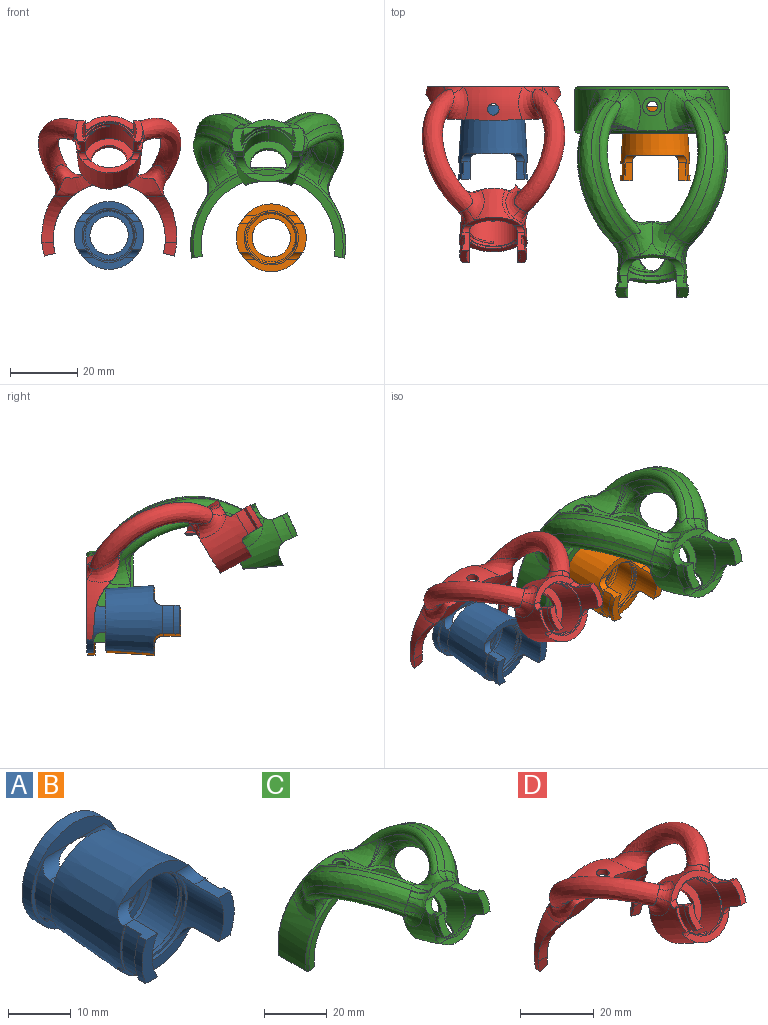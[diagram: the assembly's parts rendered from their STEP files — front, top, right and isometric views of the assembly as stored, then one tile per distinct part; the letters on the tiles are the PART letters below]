
ASSEMBLY  parts=4 mates=3
PART A: 50 faces, bbox 20.8x27.6x20.6 mm
  f0: cone r=10.29mm half-angle=3.8deg, axis (0,-1,0), area 925mm2, adj f1,f2,f13,f14,f30,f33,f40,f41
  f1: plane 8.53x1.35mm, normal (0,-1,0), area 3.4mm2, adj f0,f4,f41,f44
  f2: plane 8.53x1.35mm, normal (0,-1,0), area 3.4mm2, adj f0,f3,f40,f43
  f3: cylinder r=9.91mm len=8.53mm, axis (0,-1,0), area 30.3mm2, adj f2,f5,f40,f43
  f4: cylinder r=9.91mm len=8.53mm, axis (0,-1,0), area 30.3mm2, adj f1,f6,f41,f44
  f5: plane 8.53x1.47mm, normal (0,1,0), area 4.5mm2, adj f3,f7,f40,f43
  f6: plane 8.53x1.47mm, normal (0,1,0), area 4.5mm2, adj f4,f8,f41,f44
  f7: cylinder r=10.41mm len=8.53mm, axis (0,-1,0), area 14mm2, adj f5,f10,f40,f43
  f8: cylinder r=10.41mm len=8.53mm, axis (0,-1,0), area 14mm2, adj f6,f9,f41,f44
  f9: plane 8.53x3.56mm, normal (0,-1,0), area 20.7mm2, adj f8,f11,f41,f44
  f10: plane 8.53x3.56mm, normal (0,-1,0), area 20.7mm2, adj f7,f11,f40,f43
  f11: cylinder r=8.08mm len=16.15mm, axis (0,-1,0), area 174.9mm2, adj f9,f10,f18,f40,f41,f42,f43,f44
  f12: cone r=6.25mm half-angle=0.6deg, axis (0,1,0), area 332.4mm2, adj f15,f17,f26,f30,f31,f32,f33,f34
  f13: cylinder r=9.14mm len=12.62mm, axis (0,-1,0), area 30mm2, adj f0,f17,f32,f35,f36,f37
  f14: cylinder r=9.14mm len=12.62mm, axis (0,-1,0), area 30mm2, adj f0,f17,f31,f34,f38,f39
  f15: plane 19.81x19.81mm, normal (0,1,0), area 181.6mm2, adj f12,f16
  f16: cylinder r=9.91mm len=19.81mm, axis (0,-1,0), area 134.4mm2, adj f15,f17
  f17: plane 19.81x19.81mm, normal (0,-1,0), area 97.4mm2, adj f12,f13,f14,f16,f36,f37,f38,f39
  f18: plane 16.15x16.15mm, normal (0,-1,0), area 22.5mm2, adj f11,f19
  f19: cone r=7.61mm half-angle=0.6deg, axis (0,-1,0), area 34mm2, adj f18,f24
  f20: cylinder r=7.62mm len=15.24mm, axis (0,-1,0), area 314.7mm2, adj f24,f25,f27,f28,f29
  f21: plane 14.33x14.33mm, normal (0,-1,0), area 58.7mm2, adj f22,f25
  f22: cylinder r=5.71mm len=11.43mm, axis (0,-1,0), area 22.8mm2, adj f21,f23
  f23: cone r=5.71mm half-angle=59deg, axis (0,1,0), area 13.6mm2, adj f22,f26
  f24: cone r=7.79mm half-angle=25.9deg, axis (0,1,0), area 0.7mm2, adj f19,f20
  f25: cone r=7.17mm half-angle=45deg, axis (0,-1,0), area 29.8mm2, adj f20,f21
  f26: cone r=6.25mm half-angle=29.8deg, axis (0,1,0), area 17.1mm2, adj f12,f23
  f27: torus R=7.62mm, axis (0,-1,0), area 13.7mm2, adj f20,f28,f29
  f28: plane 0.56x0.24mm, normal (-0.5,0,-0.87), area 0.1mm2, adj f20,f27
  f29: plane 0.56x0.28mm, normal (-1,0,0), area 0.1mm2, adj f20,f27
  f30: plane 16.63x5.33mm, normal (0,1,0), area 46.3mm2, adj f0,f12,f31,f32
  f31: plane 3.3x0.93mm, normal (0,0,-1), area 3.1mm2, adj f12,f14,f30,f38
  f32: plane 3.3x0.93mm, normal (0,0,-1), area 3.1mm2, adj f12,f13,f30,f37
  f33: plane 16.63x5.33mm, normal (0,1,0), area 46.3mm2, adj f0,f12,f34,f35
  f34: plane 3.3x0.93mm, normal (0,0,1), area 3.1mm2, adj f12,f14,f33,f39
  f35: plane 3.3x0.93mm, normal (0,0,1), area 3.1mm2, adj f12,f13,f33,f36
  f36: cylinder r=2.5mm len=7.81mm, axis (1,0,0), area 14.9mm2, adj f12,f13,f17,f35
  f37: cylinder r=2.5mm len=7.81mm, axis (-1,0,0), area 14.9mm2, adj f12,f13,f17,f32
  f38: cylinder r=2.5mm len=7.81mm, axis (-1,0,0), area 14.9mm2, adj f12,f14,f17,f31
  f39: cylinder r=2.5mm len=7.81mm, axis (1,0,0), area 14.9mm2, adj f12,f14,f17,f34
  f40: plane 5.33x2.64mm, normal (0,0,-1), area 12.1mm2, adj f0,f2,f3,f5,f7,f10,f11,f47
  f41: plane 5.33x2.64mm, normal (0,0,-1), area 12.1mm2, adj f0,f1,f4,f6,f8,f9,f11,f48
  f42: plane 15.4x3.56mm, normal (0,-1,0), area 28.3mm2, adj f0,f11,f47,f48
  f43: plane 5.33x2.64mm, normal (0,0,1), area 12.1mm2, adj f0,f2,f3,f5,f7,f10,f11,f46
  f44: plane 5.33x2.64mm, normal (0,0,1), area 12.1mm2, adj f0,f1,f4,f6,f8,f9,f11,f49
  f45: plane 15.4x3.56mm, normal (0,-1,0), area 28.3mm2, adj f0,f11,f46,f49
  f46: cylinder r=2.29mm len=4.62mm, axis (1,0,0), area 9.2mm2, adj f0,f11,f43,f45
  f47: cylinder r=2.29mm len=4.62mm, axis (-1,0,0), area 9.2mm2, adj f0,f11,f40,f42
  f48: cylinder r=2.29mm len=4.62mm, axis (-1,0,0), area 9.2mm2, adj f0,f11,f41,f42
  f49: cylinder r=2.29mm len=4.62mm, axis (1,0,0), area 9.2mm2, adj f0,f11,f44,f45
PART B: same geometry as A
PART C: 129 faces, bbox 70.6x66.7x58.3 mm
  f0: bspline ~7.91x7.51mm, area 4.5mm2, adj f1,f43,f54,f119
  f1: bspline ~7.54x6.84mm, area 2.5mm2, adj f0,f2,f43,f54
  f2: bspline ~7.76x6.89mm, area 4.3mm2, adj f1,f54,f77,f121
  f3: bspline ~7.92x6.27mm, area 7.1mm2, adj f4,f7,f54,f76
  f4: bspline ~7.75x6.84mm, area 4.2mm2, adj f3,f5,f54,f76
  f5: bspline ~7.56x6.8mm, area 2.8mm2, adj f4,f46,f54,f90
  f6: bspline ~9.15x7.09mm, area 21.7mm2, adj f44,f54,f121,f124
  f7: bspline ~9.19x7.32mm, area 24.8mm2, adj f3,f48,f54,f91
  f8: cone r=10.41mm half-angle=4.7deg, axis (0,-0.91,0.41), area 0mm2, adj f39,f111,f113
  f9: cone r=10.41mm half-angle=4.7deg, axis (0,-0.91,0.41), area 136.9mm2, adj f14,f24,f39,f65,f71,f72,f101,f105
  f10: cone r=10.41mm half-angle=4.7deg, axis (0,-0.91,0.41), area 12.6mm2, adj f68,f103,f106,f107,f110,f111,f113
  f11: cylinder r=23.1mm len=12.38mm, axis (0,-1,0), area 76.2mm2, adj f49,f54,f55,f88,f119
  f12: cylinder r=23.1mm len=20.24mm, axis (0,-1,0), area 235.7mm2, adj f37,f54,f55,f81,f83,f85
  f13: cone r=10.41mm half-angle=4.7deg, axis (0,-0.91,0.41), area 137.9mm2, adj f15,f25,f39,f65,f69,f70,f92,f93
  f14: cone r=10.41mm half-angle=8.4deg, axis (0,0.91,-0.41), area 26.3mm2, adj f9,f16,f63,f66,f71,f72
  f15: cone r=10.41mm half-angle=8.4deg, axis (0,0.91,-0.41), area 26.3mm2, adj f13,f17,f64,f67,f69,f70
  f16: plane 6.7x3.05mm, normal (0,0.91,-0.41), area 6.7mm2, adj f14,f18,f63,f66
  f17: plane 6.7x3.05mm, normal (0,0.91,-0.41), area 6.7mm2, adj f15,f19,f64,f67
  f18: cylinder r=10.79mm len=7.36mm, axis (0,0.91,-0.41), area 11.9mm2, adj f16,f20,f63,f66
  f19: cylinder r=10.79mm len=7.36mm, axis (0,0.91,-0.41), area 11.9mm2, adj f17,f21,f64,f67
  f20: plane 6.7x3.55mm, normal (0,-0.91,0.41), area 20.2mm2, adj f18,f22,f63,f66
  f21: plane 6.7x3.55mm, normal (0,-0.91,0.41), area 20.2mm2, adj f19,f22,f64,f67
  f22: cylinder r=8.13mm len=18.48mm, axis (0,0.91,-0.41), area 196.6mm2, adj f20,f21,f40,f63,f64,f65,f66,f67
  f23: cylinder r=18.92mm len=12.98mm, axis (0,1,0), area 41.7mm2, adj f24,f25,f56,f57,f58,f59,f60,f61
  f24: bspline ~15.94x6.4mm, area 5.8mm2, adj f9,f23,f39,f57,f65
  f25: bspline ~15.92x6.59mm, area 5.8mm2, adj f13,f23,f39,f56,f65
  f26: cylinder r=7.75mm len=17.72mm, axis (0,0.91,-0.41), area 209.3mm2, adj f27,f38,f40,f51,f52,f53,f62
  f27: cylinder r=7.75mm len=16.78mm, axis (0,0.91,-0.41), area 140.8mm2, adj f26,f38,f51,f62
  f28: cylinder r=5.37mm len=10.73mm, axis (0,0.91,-0.41), area 34.6mm2, adj f38,f39,f58,f59
  f29: cylinder r=1.59mm len=3.18mm, axis (0,0,-1), area 25.3mm2, adj f30,f50
  f30: cone r=20.72mm half-angle=9.5deg, axis (0,1,0), area 333.4mm2, adj f29,f32,f33,f36,f37
  f31: cylinder r=23.1mm len=19.98mm, axis (0,-1,0), area 233.3mm2, adj f36,f54,f55,f123,f125,f127
  f32: cylinder r=19.93mm len=39.86mm, axis (0,-1,0), area 395.4mm2, adj f30,f35,f36,f37
  f33: cone r=19.93mm half-angle=12.9deg, axis (0,-1,0), area 253mm2, adj f30,f34,f36,f37
  f34: plane 44.69x26.22mm, normal (0,1,0), area 178mm2, adj f33,f36,f37,f55
  f35: plane 44.69x26.22mm, normal (0,-1,0), area 178mm2, adj f32,f36,f37,f54
  f36: plane 13.91x3.13mm, normal (-0.17,0,-0.98), area 40.3mm2, adj f30,f31,f32,f33,f34,f35,f54,f55
  f37: plane 13.91x3.13mm, normal (0.17,0,-0.98), area 40.3mm2, adj f12,f30,f32,f33,f34,f35,f54,f55
  f38: plane 15.5x12.02mm, normal (0,-0.91,0.41), area 76.9mm2, adj f26,f27,f28,f58,f59,f60,f61,f62
  f39: plane 20.09x15.4mm, normal (0,0.91,-0.41), area 135.6mm2, adj f8,f9,f13,f24,f25,f28,f56,f57
  f40: plane 16.26x14.8mm, normal (0,-0.91,0.41), area 19mm2, adj f22,f26
  f41: bspline ~47.72x31.38mm, area 168.5mm2, adj f79,f80,f109,f112,f127,f128
  f42: bspline ~53.98x37.41mm, area 282.1mm2, adj f78,f80,f98,f101,f102,f106,f122,f123
  f43: bspline ~47.72x31.74mm, area 181mm2, adj f0,f1,f77,f78,f113,f115,f118,f119
  f44: bspline ~42.73x31.11mm, area 149.5mm2, adj f6,f77,f79,f116,f124
  f45: bspline ~47.45x30.57mm, area 165.6mm2, adj f73,f75,f85,f87,f93,f95
  f46: bspline ~47.45x30.94mm, area 177.5mm2, adj f5,f74,f76,f86,f88,f90,f108,f111
  f47: bspline ~53.68x36.56mm, area 277.5mm2, adj f73,f74,f81,f82,f94,f96,f99,f103
  f48: bspline ~42.49x30.37mm, area 146.6mm2, adj f7,f75,f76,f91,f100
  f49: cylinder r=2.79mm len=5.59mm, axis (0,0,1), area 7.3mm2, adj f11,f50
  f50: plane 5.59x5.59mm, normal (0,0,1), area 16.6mm2, adj f29,f49
  f51: torus R=7.75mm, axis (0,0.91,-0.41), area 26.8mm2, adj f26,f27,f52,f53,f62
  f52: plane 0.71x0.68mm, normal (1,0,0), area 0.3mm2, adj f26,f51,f62
  f53: plane 0.68x0.5mm, normal (1,0,0), area 0.2mm2, adj f26,f51
  f54: cone r=22.34mm half-angle=45deg, axis (0,1,0), area 85.5mm2, adj f0,f1,f2,f3,f4,f5,f6,f7
  f55: cone r=23.1mm half-angle=45deg, axis (0,-1,0), area 85.5mm2, adj f11,f12,f31,f34,f36,f37,f82,f84
  f56: bspline ~4.11x1.37mm, area 2.2mm2, adj f23,f25,f39,f58
  f57: bspline ~4.11x1.37mm, area 2.2mm2, adj f23,f24,f39,f59
  f58: bspline ~3x2.35mm, area 1.3mm2, adj f23,f28,f38,f39,f56,f60
  f59: bspline ~2.61x2.21mm, area 1.3mm2, adj f23,f28,f38,f39,f57,f61
  f60: bspline ~3.63x1.5mm, area 3mm2, adj f23,f38,f58,f62
  f61: bspline ~3.63x1.5mm, area 3mm2, adj f23,f38,f59,f62
  f62: bspline ~12.66x10.62mm, area 23.2mm2, adj f23,f26,f27,f38,f51,f52,f60,f61
  f63: plane 3.47x2.9mm, normal (0,-0.41,-0.91), area 9.3mm2, adj f14,f16,f18,f20,f22,f71
  f64: plane 3.47x2.9mm, normal (0,-0.41,-0.91), area 9.3mm2, adj f15,f17,f19,f21,f22,f70
  f65: plane 13.91x2.36mm, normal (0,-0.91,0.41), area 22.3mm2, adj f9,f13,f22,f23,f24,f25,f70,f71
  f66: plane 3.47x2.9mm, normal (0,0.41,0.91), area 9.3mm2, adj f14,f16,f18,f20,f22,f72
  f67: plane 3.47x2.9mm, normal (0,0.41,0.91), area 9.3mm2, adj f15,f17,f19,f21,f22,f69
  f68: plane 14x2.63mm, normal (0,-0.91,0.41), area 23mm2, adj f10,f22,f69,f72,f99,f102
  f69: cylinder r=3.81mm len=6.52mm, axis (1,0,0), area 15.7mm2, adj f13,f15,f22,f67,f68,f96
  f70: cylinder r=3.81mm len=6.52mm, axis (-1,0,0), area 14.5mm2, adj f13,f15,f22,f64,f65
  f71: cylinder r=3.81mm len=6.52mm, axis (-1,0,0), area 14.5mm2, adj f9,f14,f22,f63,f65
  f72: cylinder r=3.81mm len=6.52mm, axis (1,0,0), area 15.6mm2, adj f9,f14,f22,f66,f68,f98
  f73: bspline ~43.13x18.49mm, area 113.9mm2, adj f45,f47,f83,f92
  f74: bspline ~42.95x17.71mm, area 117.2mm2, adj f46,f47,f84,f107
  f75: bspline ~28.39x8.95mm, area 68.2mm2, adj f45,f48,f89,f97
  f76: bspline ~27.12x9.68mm, area 67mm2, adj f3,f4,f46,f48,f104
  f77: bspline ~29.25x10.37mm, area 68.8mm2, adj f2,f43,f44,f117,f121
  f78: bspline ~43.34x18.52mm, area 119.1mm2, adj f42,f43,f110,f120
  f79: bspline ~28.61x9.19mm, area 69.1mm2, adj f41,f44,f114,f126
  f80: bspline ~42.92x18.13mm, area 115.8mm2, adj f41,f42,f105,f125
  f81: bspline ~7.6x7.02mm, area 14.3mm2, adj f12,f47,f82,f83
  f82: bspline ~7.86x7.49mm, area 27.6mm2, adj f47,f55,f81,f84
  f83: bspline ~6.87x5.38mm, area 9.3mm2, adj f12,f73,f81,f85
  f84: bspline ~4.06x3.75mm, area 6.9mm2, adj f55,f74,f82,f86
  f85: bspline ~11.34x8.59mm, area 45.3mm2, adj f12,f45,f83,f87
  f86: bspline ~5.71x4.29mm, area 12.1mm2, adj f46,f55,f84,f88
  f87: bspline ~9.93x4.5mm, area 20.1mm2, adj f45,f54,f85,f89
  f88: bspline ~14.41x8.96mm, area 71mm2, adj f11,f46,f86,f90
  f89: bspline ~6.71x4.76mm, area 10.5mm2, adj f54,f75,f87,f91
  f90: bspline ~7.71x7.56mm, area 5.1mm2, adj f5,f46,f54,f88
  f91: bspline ~7.82x6.21mm, area 19.7mm2, adj f7,f48,f54,f89
  f92: bspline ~6.29x4.12mm, area 9.4mm2, adj f13,f73,f93,f94
  f93: bspline ~9.66x8.82mm, area 43.9mm2, adj f13,f45,f92,f95
  f94: bspline ~6.66x4.13mm, area 9.2mm2, adj f13,f47,f92,f96
  f95: bspline ~7.01x4.77mm, area 9.4mm2, adj f39,f45,f93,f97
  f96: bspline ~7.08x4.06mm, area 13.4mm2, adj f47,f69,f94,f99
  f97: bspline ~5.37x5.05mm, area 9.5mm2, adj f39,f75,f95,f100
  f98: bspline ~7.31x4.46mm, area 13.7mm2, adj f42,f72,f101,f102
  f99: bspline ~6.46x6.38mm, area 15.1mm2, adj f47,f68,f96,f103
  f100: bspline ~10.17x8.87mm, area 27.9mm2, adj f39,f48,f97,f104
  f101: bspline ~6.66x3.88mm, area 8.3mm2, adj f9,f42,f98,f105
  f102: bspline ~6.6x6.53mm, area 15.8mm2, adj f42,f68,f98,f106
  f103: bspline ~6.53x5.37mm, area 2.5mm2, adj f10,f47,f99,f107
  f104: bspline ~6.07x4.08mm, area 9.5mm2, adj f39,f76,f100,f108
  f105: bspline ~6.35x5.04mm, area 9.6mm2, adj f9,f80,f101,f109
  f106: bspline ~5.77x4.86mm, area 1.1mm2, adj f10,f42,f102,f110
  f107: bspline ~7.15x4.53mm, area 9.5mm2, adj f10,f74,f103,f111
  f108: bspline ~7.96x4.46mm, area 9.4mm2, adj f39,f46,f104,f111
  f109: bspline ~9.67x8.81mm, area 45.1mm2, adj f9,f41,f105,f112
  f110: bspline ~6.67x5.05mm, area 9.6mm2, adj f10,f78,f106,f113
  f111: bspline ~10.49x6.33mm, area 41.3mm2, adj f8,f10,f46,f107,f108,f113
  f112: bspline ~7.08x4.83mm, area 9.7mm2, adj f39,f41,f109,f114
  f113: bspline ~11.12x6.82mm, area 42.5mm2, adj f8,f10,f43,f110,f111,f115
  f114: bspline ~5.09x4.79mm, area 9.7mm2, adj f39,f79,f112,f116
  f115: bspline ~7.9x4.55mm, area 9.7mm2, adj f39,f43,f113,f117
  f116: bspline ~10.09x8.84mm, area 29.6mm2, adj f39,f44,f114,f117
  f117: bspline ~6.29x4.96mm, area 9.7mm2, adj f39,f77,f115,f116
  f118: bspline ~5.86x4.09mm, area 12.4mm2, adj f43,f55,f119,f120
  f119: bspline ~14.26x8.7mm, area 71.8mm2, adj f0,f11,f43,f118
  f120: bspline ~3.43x3.3mm, area 6.5mm2, adj f55,f78,f118,f122
  f121: bspline ~7.95x6.31mm, area 7.4mm2, adj f2,f6,f54,f77
  f122: bspline ~7.96x7.72mm, area 27.3mm2, adj f42,f55,f120,f123
  f123: bspline ~6.94x6.87mm, area 12.4mm2, adj f31,f42,f122,f125
  f124: bspline ~8.69x6.97mm, area 24.1mm2, adj f6,f44,f54,f126
  f125: bspline ~6.21x5.21mm, area 9.4mm2, adj f31,f80,f123,f127
  f126: bspline ~7.06x5.14mm, area 11.1mm2, adj f54,f79,f124,f128
  f127: bspline ~10.63x8.37mm, area 47.5mm2, adj f31,f41,f125,f128
  f128: bspline ~10.46x5.25mm, area 20.7mm2, adj f41,f54,f126,f127
PART D: 69 faces, bbox 52.4x58.9x55 mm
  f0: cone r=10.08mm half-angle=3.9deg, axis (0,-0.86,0.52), area 72.8mm2, adj f1,f2,f3,f4
  f1: plane 17x4.13mm, normal (0,-0.86,0.52), area 32.1mm2, adj f0,f5,f6,f7,f8,f9
  f2: bspline ~10.12x5.82mm, area 36.4mm2, adj f0,f9,f10,f11
  f3: plane 19.26x16.6mm, normal (0,0.86,-0.52), area 177.7mm2, adj f0,f10,f12,f13,f14
  f4: bspline ~9.77x5.55mm, area 36.5mm2, adj f0,f5,f13,f15
  f5: bspline ~5.09x4.16mm, area 13.6mm2, adj f1,f4,f12,f15,f16
  f6: cylinder r=1.52mm len=3.13mm, axis (1,0,0), area 5.3mm2, adj f1,f7,f12,f17
  f7: cylinder r=8.05mm len=18.05mm, axis (0,0.86,-0.52), area 148.4mm2, adj f1,f6,f8,f17,f18,f19,f20,f21
  f8: cylinder r=1.52mm len=3.13mm, axis (1,0,0), area 5mm2, adj f1,f7,f9,f12,f19
  f9: bspline ~5.16x4.3mm, area 14.2mm2, adj f1,f2,f8,f11,f12,f27
  f10: bspline ~7.81x7.49mm, area 26.7mm2, adj f2,f3,f11,f27
  f11: bspline ~36.98x22.5mm, area 715.1mm2, adj f2,f9,f10,f27,f28,f29
  f12: cone r=10.08mm half-angle=3.9deg, axis (0,-0.86,0.52), area 411.6mm2, adj f3,f5,f6,f8,f9,f16,f17,f19
  f13: bspline ~7.86x7.5mm, area 26.8mm2, adj f3,f4,f15,f16
  f14: cylinder r=5.29mm len=10.58mm, axis (0,0.86,-0.52), area 39.6mm2, adj f3,f32
  f15: bspline ~36.8x22.34mm, area 707.1mm2, adj f4,f5,f13,f16,f33,f34
  f16: bspline ~9.26x7.73mm, area 38mm2, adj f5,f12,f13,f15
  f17: plane 5.23x3.17mm, normal (0,0.52,0.86), area 10.3mm2, adj f6,f7,f12,f26,f31,f35,f36,f37
  f18: plane 16.1x13.78mm, normal (0,-0.86,0.52), area 18.8mm2, adj f7,f38
  f19: plane 5.23x3.17mm, normal (0,0.52,0.86), area 10.3mm2, adj f7,f8,f12,f20,f30,f39,f40,f41
  f20: plane 6.17x3.73mm, normal (0,-0.86,0.52), area 14.1mm2, adj f7,f19,f21,f39
  f21: plane 5.23x3.17mm, normal (0,-0.52,-0.86), area 10.3mm2, adj f7,f12,f20,f22,f30,f39,f40,f41
  f22: cylinder r=1.52mm len=3.13mm, axis (-1,0,0), area 5.3mm2, adj f7,f12,f21,f23
  f23: plane 16.95x4.09mm, normal (0,-0.86,0.52), area 32.1mm2, adj f7,f12,f22,f24
  f24: cylinder r=1.52mm len=3.13mm, axis (-1,0,0), area 5.3mm2, adj f7,f12,f23,f25
  f25: plane 5.23x3.17mm, normal (0,-0.52,-0.86), area 10.3mm2, adj f7,f12,f24,f26,f31,f35,f36,f37
  f26: plane 6.17x3.73mm, normal (0,-0.86,0.52), area 14.1mm2, adj f7,f17,f25,f37
  f27: bspline ~13.08x10.31mm, area 180.8mm2, adj f9,f10,f11,f12,f42
  f28: bspline ~6.2x5.73mm, area 13.6mm2, adj f11,f29,f43
  f29: bspline ~12.8x9.87mm, area 105.9mm2, adj f11,f28,f44,f45,f46,f47
  f30: plane 6.17x3.73mm, normal (0,-0.86,0.52), area 6.6mm2, adj f12,f19,f21,f41
  f31: plane 6.17x3.73mm, normal (0,-0.86,0.52), area 6.6mm2, adj f12,f17,f25,f35
  f32: plane 15.34x13.13mm, normal (0,-0.86,0.52), area 97mm2, adj f14,f38
  f33: bspline ~6.06x5.59mm, area 13.6mm2, adj f15,f34,f43
  f34: bspline ~12.97x9.88mm, area 105.6mm2, adj f15,f33,f46,f47,f48,f49
  f35: cylinder r=9.19mm len=7.55mm, axis (0,0.86,-0.52), area 19.8mm2, adj f17,f25,f31,f36
  f36: cone r=9.19mm half-angle=45deg, axis (0,-0.86,0.52), area 8mm2, adj f17,f25,f35,f37
  f37: cylinder r=9.96mm len=6.99mm, axis (0,0.86,-0.52), area 11.7mm2, adj f17,f25,f26,f36
  f38: cylinder r=7.67mm len=17.65mm, axis (0,0.86,-0.52), area 404.3mm2, adj f18,f32,f50,f51,f52,f53,f54,f55
  f39: cylinder r=9.96mm len=6.99mm, axis (0,0.86,-0.52), area 11.7mm2, adj f19,f20,f21,f40
  f40: cone r=9.19mm half-angle=45deg, axis (0,-0.86,0.52), area 8mm2, adj f19,f21,f39,f41
  f41: cylinder r=9.19mm len=7.55mm, axis (0,0.86,-0.52), area 19.8mm2, adj f19,f21,f30,f40
  f42: bspline ~43.05x38.8mm, area 22.3mm2, adj f27
  f43: plane 39.5x25.01mm, normal (0,1,0), area 110.1mm2, adj f28,f33,f44,f47,f49,f57,f58,f59
  f44: revolved ~18.88x7.37mm, area 62.6mm2, adj f29,f43,f45,f57,f60
  f45: extruded ~13.73x9.23mm, area 62.4mm2, adj f29,f44,f46,f60,f61
  f46: extruded ~32.63x7.8mm, area 124.3mm2, adj f29,f34,f45,f47,f48,f61,f62,f63
  f47: revolved ~18.77x9.87mm, area 153.3mm2, adj f29,f34,f43,f46,f65
  f48: extruded ~13.73x9.23mm, area 62.4mm2, adj f34,f46,f49,f61,f66
  f49: revolved ~19.01x7.39mm, area 63.2mm2, adj f34,f43,f48,f59,f66
  f50: bspline ~2.64x2.2mm, area 0.4mm2, adj f38,f51,f54,f67
  f51: torus R=7.67mm, axis (0,0.86,-0.52), area 21.9mm2, adj f38,f50,f52,f53
  f52: plane 0.59x0.48mm, normal (1,0,0), area 0.2mm2, adj f38,f51
  f53: plane 0.59x0.48mm, normal (1,0,0), area 0.2mm2, adj f38,f51
  f54: plane 2.52x2.17mm, normal (0,0.86,-0.52), area 1.3mm2, adj f38,f50,f67
  f55: bspline ~2.29x2.14mm, area 0mm2, adj f38,f56
  f56: plane 3.53x3.31mm, normal (0,0.86,-0.52), area 0.4mm2, adj f38,f55
  f57: plane 3.22x1.85mm, normal (-0.26,0,-0.97), area 4.8mm2, adj f43,f44,f58,f60,f61
  f58: cone r=17.95mm half-angle=45deg, axis (0,1,0), area 114mm2, adj f43,f57,f59,f61
  f59: plane 3.22x1.85mm, normal (0.26,0,-0.97), area 4.8mm2, adj f43,f49,f58,f61,f66
  f60: plane 4.08x3.99mm, normal (0,-0.99,-0.11), area 12.6mm2, adj f44,f45,f57,f61
  f61: cylinder r=16.68mm len=33.35mm, axis (0,-1,0), area 190.6mm2, adj f45,f46,f48,f57,f58,f59,f60,f62
  f62: plane 7.79x2.84mm, normal (0.87,0,-0.5), area 18.1mm2, adj f46,f61,f64,f68
  f63: plane 7.79x2.84mm, normal (-0.87,0,-0.5), area 18.1mm2, adj f46,f61,f64,f68
  f64: cylinder r=18.83mm len=7.88mm, axis (0,1,0), area 28mm2, adj f46,f62,f63,f65,f68
  f65: cylinder r=1.71mm len=3.43mm, axis (0,0,-1), area 19.4mm2, adj f47,f64,f68
  f66: plane 4.08x3.99mm, normal (0,-0.99,-0.11), area 12.6mm2, adj f48,f49,f59,f61
  f67: plane 2.39x2.04mm, normal (0.71,-0.33,-0.62), area 1.2mm2, adj f50,f54
  f68: cone r=18.83mm half-angle=35.9deg, axis (0,-1,0), area 35.4mm2, adj f61,f62,f63,f64,f65
PLACE A t=(-48.35,2.43,-12.8)mm
PLACE B t=(-0.03,2.05,-13.52)mm
PLACE C t=(-0.96,14.24,-15.53)mm
PLACE D t=(-48.28,9.44,-13.78)mm fixed
MATE planar D.f43 <-> C.f34  axis (0,1,0) through (-48.28,7.51,-3.89)mm
MATE planar B.f27 <-> C.f11  axis (0,1,0) through (-0.03,7.13,-13.52)mm
MATE planar A.f27 <-> D.f43  axis (0,1,0) through (-48.35,7.51,-12.8)mm
